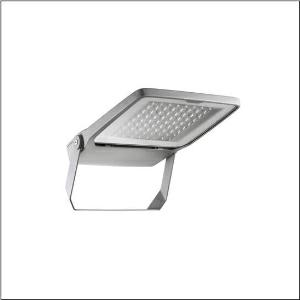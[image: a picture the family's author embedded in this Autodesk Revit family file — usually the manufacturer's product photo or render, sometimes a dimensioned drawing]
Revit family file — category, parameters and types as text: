
# Revit family: floodlight_fl_20_mini___pl43_5xa7671c2a1kc_5759
name_source: partatom
category: Lighting Fixtures
units: mm (PartAtom-declared; Revit-internal decimal feet)

## family parameters
Cut with Voids When Loaded = No
Host = Face
Light Source = No
Part Type = Normal
Room Calculation Point = No
Round Connector Dimension = Use Diameter
Shared = No

## types (1)
- Floodlight FL 20 mini  PL43 (1 x LED 4000K / CRI = 70 (unbekannt), 13030 lm, 4000K)
    Apparent Load = 96 VA
    CIE Flux Codes = 32 74 99 100 100
    Color Rendering = 70
    Color Temperature = 4000K
    Default Elevation = 1800 mm
    Description = Floodlight FL 20 mini, floodlight, primary light control with lens, of plastic, primary optical cover: protective disc, of toughened safety glass, transparent, light distribution: PL43, light emission: direct distribution, primary light characteristic: asymmetric, installation type: surface-mounted, LED, High Power LED, rated luminous flux: 13.030lm, luminous efficacy: 136lm/W, light colour: 740, colour temperature: 4000K, control gear: ECG Basic, control: power reduction, overheat protection, electronic power reduction, with terminal, 5-pole, max. 2.5mm², mains connection: 220..240V, AC, 50/60Hz, rated input power: 96W, LED unit, of diecast aluminium, powder-coated, Siteco® metallic grey (DB 702S), corrosivity category C5 mid according to DIN EN ISO 12944, incl. 1x M20 cable gland for cable Ø 6.5..12mm, length: 446mm, width: 355mm, height: 62mm, housing frame, of diecast aluminium, powder-coated, Siteco® metallic grey (DB 702S), mounting bracket, of steel, powder-coated, Siteco® metallic grey (DB 702S), ON/OFF, protection rating (complete): IP66, insulation class (complete): insulation class I (protective earthing), certification: CE, ENEC, VDE, protection symbol: D, permissible operating ambient temperature: -40..+40°C, permissible operating ambient temperature for outdoor applications: -40..+50°C, standard: DIN EN 12944, packaging unit: 1 piece

Light Distribution: PL43
    Height = 62 mm  [stored 0.203412 ft]
    Lamp = 1 x LED 4000K / CRI >= 70 (unbekannt)
    Lamp Light Flux = 13030 lm
    Lamp count = 1
    Length = 467 mm
    Luminous efficacy = 136 lm/W
    Manufacturer = Siteco
    ModVariant = No
    Model = 5XA7671C2A1KC
    Mounting Place = Wall
    Mounting Type = Surface mounted
    Number of Poles = 1
    OnlyDefault = Yes
    Power Factor = 1
    Product Name = Floodlight FL 20 mini | PL43
    Product group = floodlight | wall mounted
    ProductGroupID = 2001
    Protection Class = Protection class I
    Protection Degree = IP 66
    RLX_Detail_Level = 1
    RLX_Emergency_Light_Flux = 0 lm
    RLX_Emergency_Type = 0
    RLX_Emergency_Type_DB = No
    RlxData = <blob elided: 70881 chars, md5=b2af5d56>
    Socket = socket
    Standby Power = 0 W
    System Light Flux = 13030 lm
    System Power = 96 W
    Type Comments = Product without accessories
    Type Image = l_1005948.jpg
    URL = http://relux.com
    VarID = ---
    Voltage = 0 V
    Weight = 0.00 kg
    Width = 335 mm

note: [stored X ft] marks values corroborated as IEEE doubles in the binary element streams (Revit-internal decimal feet)

## geometry (parser evidence)
native form markers: Blend x4, Sweep x11
no freeform markers — native parametric forms only
